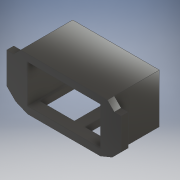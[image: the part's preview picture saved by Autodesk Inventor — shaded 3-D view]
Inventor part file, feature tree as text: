
AUTODESK INVENTOR PART (.ipt)
format: ipt  version: 2018 (Build 220112000, 112)  size: 164,864 bytes
history: native  units: mm
features: extrude x3, sketch x3, chamfer x2, shell x1, projected_geometry x1
ambient origin geometry x8: Origin, YZ Plane, XZ Plane, XY Plane, X Axis, Y Axis, Z Axis, Center Point
bodies: 实体1 (feature_tree)
feature tree (10):
  extrude  "拉伸1"  Depth=15.0mm
  shell  "抽壳1"  Thickness=25.0mm
  extrude  "拉伸2"  Depth=7.0mm
  extrude  "拉伸3"  Depth=3.0mm
  chamfer  "倒角1"  Distance=2.5mm
  chamfer  "倒角2"  Distance=5.0mm
  sketch  "草图1"  dims[d0=15.0mm d1=0.0mm d2=15.0mm d3=25.0mm]
  sketch  "草图2"  dims[d4=2.0mm d5=7.0mm]
  sketch  "草图3"  dims[d6=4.5mm d7=3.0mm d8=2.5mm d9=5.0mm d10=0.0mm d11=10.0mm d12=10.0mm d13=3.0mm d14=2.5mm d15=4.0mm d16=11.0mm d17=2.0mm d18=0.0mm d19=2.0mm d20=2.0mm d21=45.0deg d22=2.0mm d23=2.0mm d24=45.0deg]
  projected_geometry  "投影回路1"
